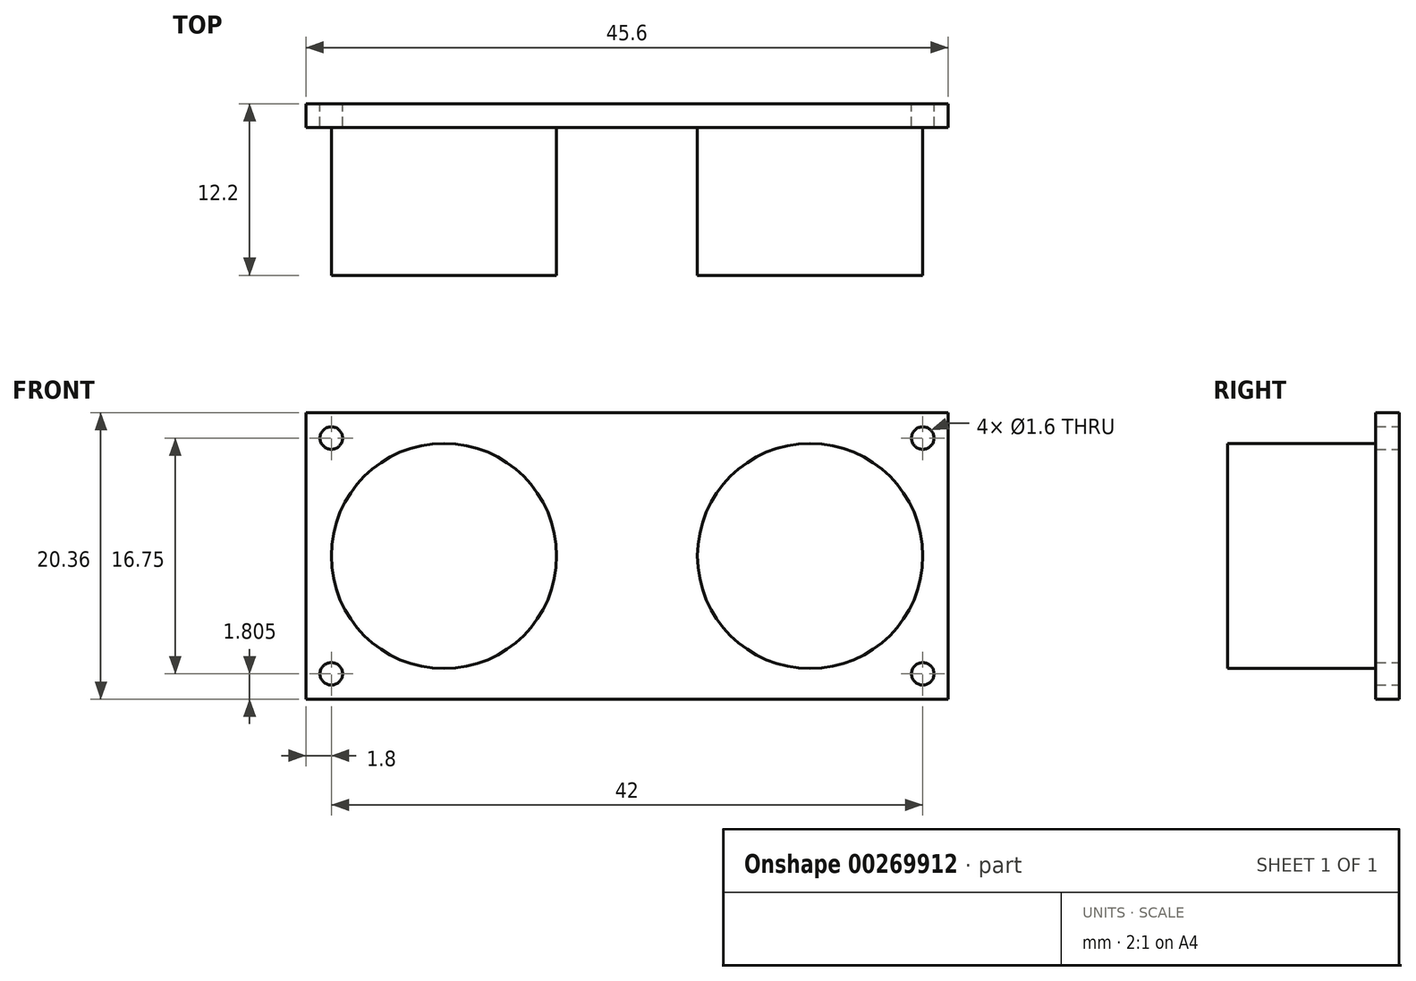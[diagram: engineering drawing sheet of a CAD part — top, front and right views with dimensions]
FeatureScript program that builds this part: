
annotation { "Feature Type Name" : "Feature", "Feature Type Description" : "" }
export const myFeature = defineFeature(function(context is Context, id is Id, definition is map)
    precondition{}
    {
        {
            var Q0;
            Q0=qCreatedBy(makeId("Front.planeOp"),FACE);
            var sketch = newSketch(context, id + "F0", { "sketchPlane" : qUnion([Q0])});
            skLineSegment(sketch, "E0.bottom", {"start": v(-22.8, 10.18) * mm, "end": v(22.8, 10.18) * mm});
            skLineSegment(sketch, "E0.top", {"start": v(-22.8, -10.18) * mm, "end": v(22.8, -10.18) * mm});
            skLineSegment(sketch, "E0.left", {"start": v(-22.8, 10.18) * mm, "end": v(-22.8, -10.18) * mm});
            skLineSegment(sketch, "E0.right", {"start": v(22.8, 10.18) * mm, "end": v(22.8, -10.18) * mm});
            skCircle(sketch, "E1", {"center": v(13, 0) * mm, "radius": 8 * mm});
            skCircle(sketch, "E2", {"center": v(-13, 0) * mm, "radius": 8 * mm});
            skCircle(sketch, "E3", {"center": v(-21, -8.38) * mm, "radius": 0.8 * mm});
            skCircle(sketch, "E4.MirrorC", {"center": v(21, -8.38) * mm, "radius": 0.8 * mm});
            skCircle(sketch, "E5.MirrorC", {"center": v(-21, 8.38) * mm, "radius": 0.8 * mm});
            skCircle(sketch, "E6.MirrorC", {"center": v(21, 8.38) * mm, "radius": 0.8 * mm});
            skSolve(sketch);
        }
        {
            var Q0;
            Q0=makeQuery(id+"F0.imprint","IMPRINT",FACE,{"disambiguationData":[TD([[makeQuery(id+"F0.imprint","IMPRINT",EDGE,{"derivedFrom":sQuery(id+"F0.wireOp",EDGE,"E0.bottom")}),-1.0]])]});
            extrude(context, id + "F1", {"entities" : qUnion([Q0]), "depth" : 1.7 * mm});
        }
        {
            var Q0;
            Q0=makeQuery(id+"F0.imprint","IMPRINT",FACE,{"disambiguationData":[TD([[makeQuery(id+"F0.imprint","IMPRINT",EDGE,{"derivedFrom":sQuery(id+"F0.wireOp",EDGE,"E2")}),1.0]])]});
            var Q1;
            Q1=makeQuery(id+"F0.imprint","IMPRINT",FACE,{"disambiguationData":[TD([[makeQuery(id+"F0.imprint","IMPRINT",EDGE,{"derivedFrom":sQuery(id+"F0.wireOp",EDGE,"E1")}),1.0]])]});
            extrude(context, id + "F2", {"entities" : qUnion([Q0, Q1]), "operationType" : NewBodyOperationType.ADD, "depth" : 12.2 * mm});
        }
    });
